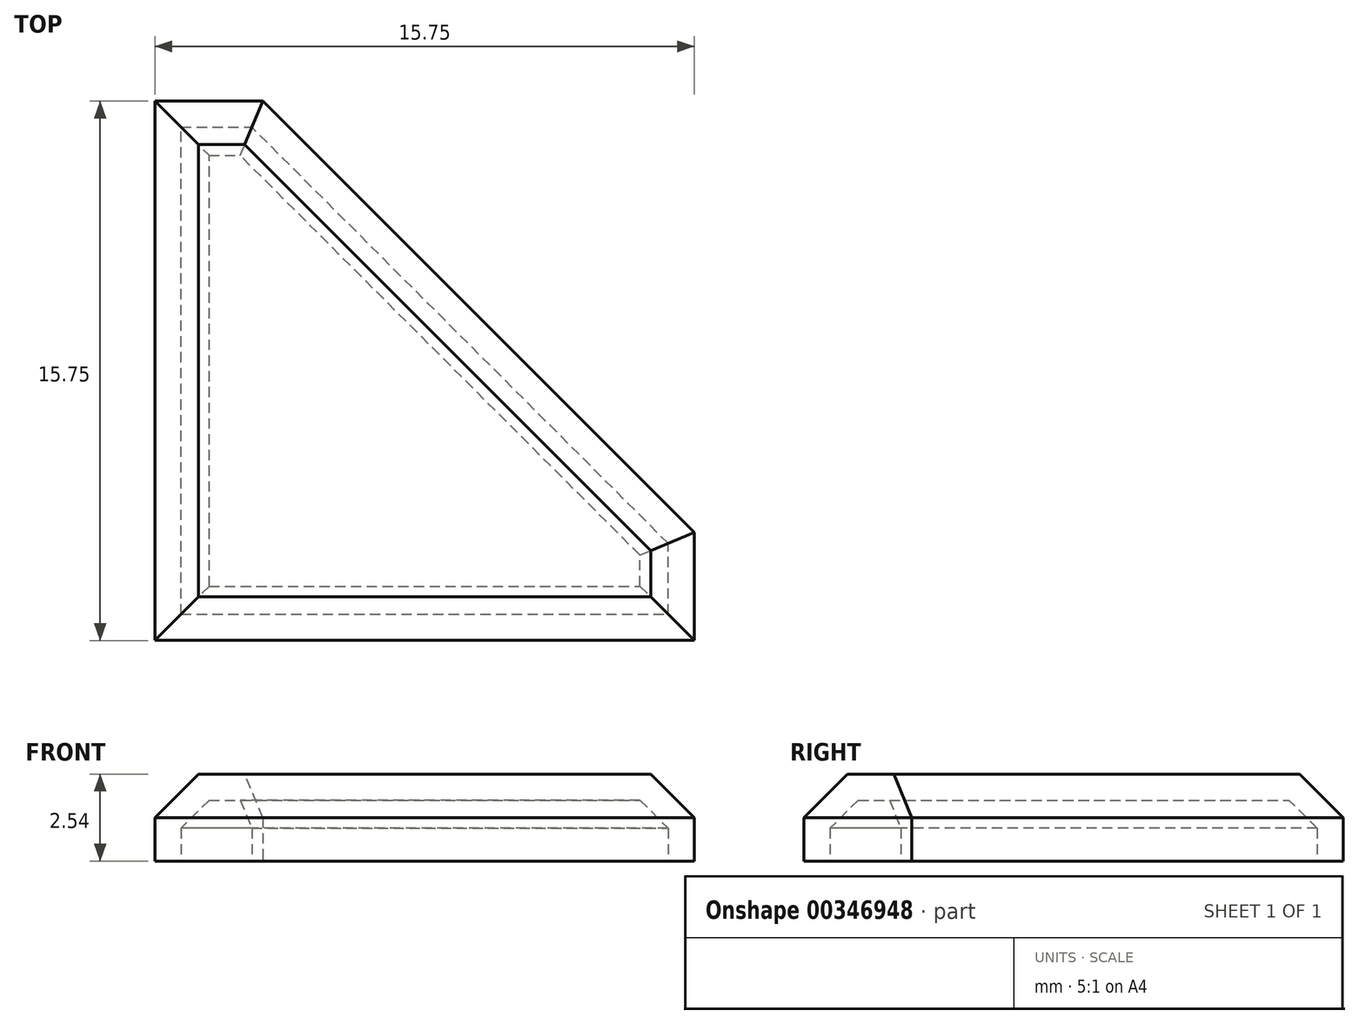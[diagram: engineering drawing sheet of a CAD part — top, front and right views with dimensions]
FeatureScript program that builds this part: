
annotation { "Feature Type Name" : "Feature", "Feature Type Description" : "" }
export const myFeature = defineFeature(function(context is Context, id is Id, definition is map)
    precondition{}
    {
        {
            var Q0;
            Q0=qCreatedBy(makeId("Top.planeOp"),FACE);
            var sketch = newSketch(context, id + "F0", { "sketchPlane" : qUnion([Q0])});
            skLineSegment(sketch, "E0.bottom", {"start": v(-47.24, -56.79) * mm, "end": v(-31.5, -56.79) * mm});
            skLineSegment(sketch, "E0.left", {"start": v(-47.24, -56.79) * mm, "end": v(-47.24, -41.04) * mm});
            skLineSegment(sketch, "E1", {"start": v(-47.24, -41.04) * mm, "end": v(-44.1, -41.04) * mm});
            skLineSegment(sketch, "E2", {"start": v(-31.5, -56.79) * mm, "end": v(-31.5, -53.64) * mm});
            skLineSegment(sketch, "E3", {"start": v(-31.5, -53.64) * mm, "end": v(-44.1, -41.04) * mm});
            skSolve(sketch);
        }
        {
            var Q0;
            Q0=makeQuery(id+"F0.imprint","IMPRINT",FACE,{"disambiguationData":[TD([[makeQuery(id+"F0.imprint","IMPRINT",EDGE,{"derivedFrom":sQuery(id+"F0.wireOp",EDGE,"E0.bottom")}),1.0]])]});
            extrude(context, id + "F1", {"entities" : qUnion([Q0]), "depth" : 2.54 * mm});
        }
        {
            var Q0;
            Q0=makeQuery(id+"F1.opExtrude","CAP_FACE",FACE,{"disambiguationData":[OSD([sQuery(id+"F0.wireOp",EDGE,"E0.bottom"),sQuery(id+"F0.wireOp",EDGE,"E0.left"),sQuery(id+"F0.wireOp",EDGE,"E1"),sQuery(id+"F0.wireOp",EDGE,"E2"),sQuery(id+"F0.wireOp",EDGE,"E3")])],"isStart":false});
            chamfer(context, id + "F2", {"entities" : qUnion([Q0]), "width" : 1.27 * mm, "tangentPropagation" : true});
        }
        {
            var Q0;
            Q0=makeQuery(id+"F1.opExtrude","CAP_FACE",FACE,{"disambiguationData":[OSD([sQuery(id+"F0.wireOp",EDGE,"E0.bottom"),sQuery(id+"F0.wireOp",EDGE,"E0.left"),sQuery(id+"F0.wireOp",EDGE,"E1"),sQuery(id+"F0.wireOp",EDGE,"E2"),sQuery(id+"F0.wireOp",EDGE,"E3")])],"isStart":true});
            shell(context, id + "F3", {"entities" : qUnion([Q0]), "thickness" : 0.76 * mm});
        }
    });
